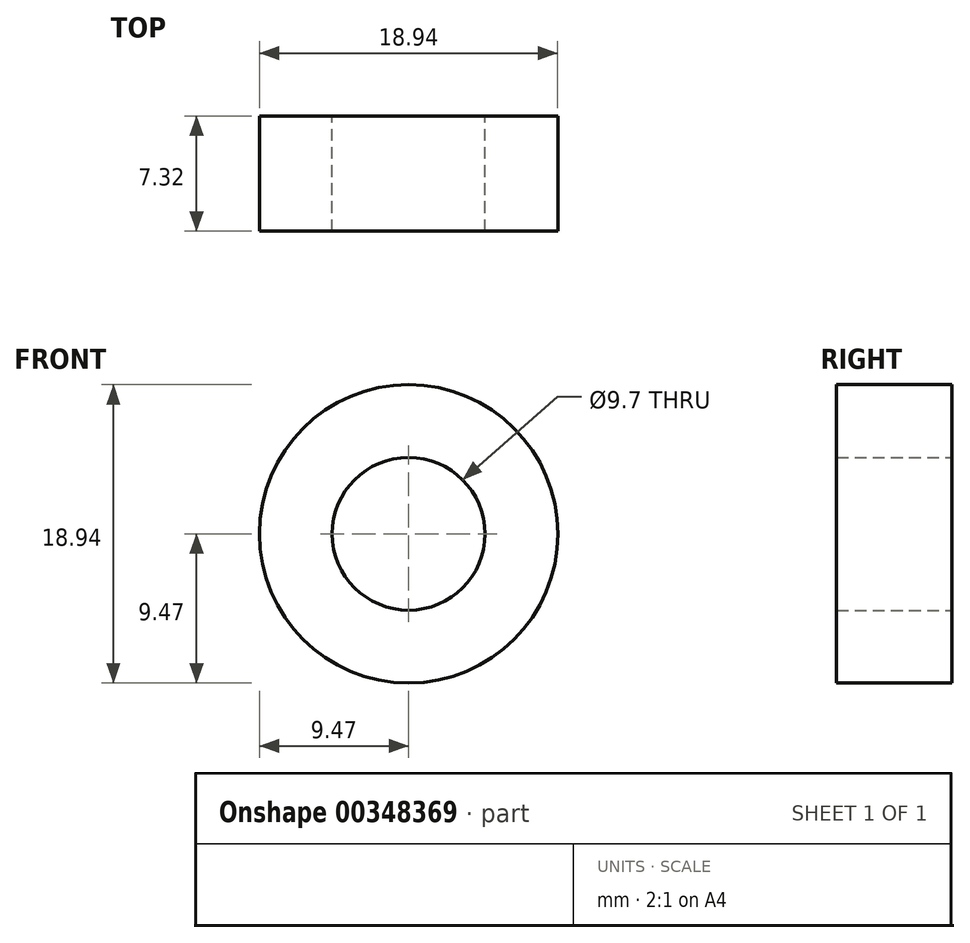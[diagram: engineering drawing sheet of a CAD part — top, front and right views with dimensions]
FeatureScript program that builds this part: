
annotation { "Feature Type Name" : "Feature", "Feature Type Description" : "" }
export const myFeature = defineFeature(function(context is Context, id is Id, definition is map)
    precondition{}
    {
        {
            var Q0;
            Q0=qCreatedBy(makeId("Front.planeOp"),FACE);
            var sketch = newSketch(context, id + "F0", { "sketchPlane" : qUnion([Q0])});
            skCircle(sketch, "E0", {"center": v(0, 0) * mm, "radius": 9.47 * mm});
            skCircle(sketch, "E1", {"center": v(0, 0) * mm, "radius": 4.85 * mm});
            skSolve(sketch);
        }
        {
            var Q0;
            Q0=makeQuery(id+"F0.imprint","IMPRINT",FACE,{"disambiguationData":[TD([[makeQuery(id+"F0.imprint","IMPRINT",EDGE,{"derivedFrom":sQuery(id+"F0.wireOp",EDGE,"E0")}),1.0]])]});
            extrude(context, id + "F1", {"entities" : qUnion([Q0]), "depth" : 7.32 * mm});
        }
    });
